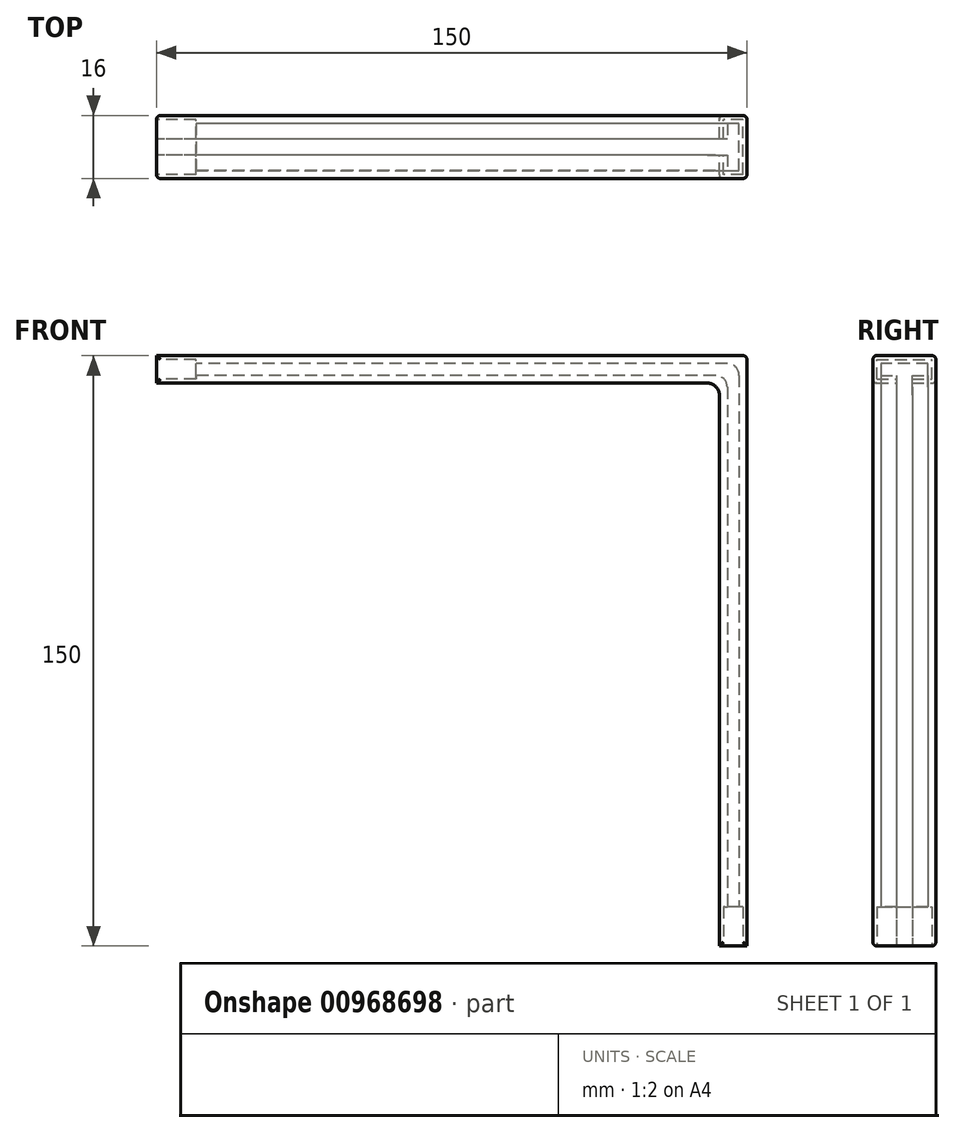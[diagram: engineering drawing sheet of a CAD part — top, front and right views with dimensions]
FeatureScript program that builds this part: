
annotation { "Feature Type Name" : "Feature", "Feature Type Description" : "" }
export const myFeature = defineFeature(function(context is Context, id is Id, definition is map)
    precondition{}
    {
        {
            var Q0;
            Q0=qCreatedBy(makeId("Front.planeOp"),FACE);
            var sketch = newSketch(context, id + "F0", { "sketchPlane" : qUnion([Q0])});
            skLineSegment(sketch, "E0", {"start": v(-19.44, 7) * mm, "end": v(130.56, 7) * mm});
            skLineSegment(sketch, "E1", {"start": v(130.56, 7) * mm, "end": v(130.56, -143) * mm});
            skLineSegment(sketch, "E2", {"start": v(130.56, -143) * mm, "end": v(123.56, -143) * mm});
            skLineSegment(sketch, "E3", {"start": v(123.56, -143) * mm, "end": v(123.56, 0) * mm});
            skLineSegment(sketch, "E4", {"start": v(123.56, 0) * mm, "end": v(-19.44, 0) * mm});
            skLineSegment(sketch, "E5", {"start": v(-19.44, 0) * mm, "end": v(-19.44, 7) * mm});
            skSolve(sketch);
        }
        {
            var Q0;
            Q0=makeQuery(id+"F0.imprint","IMPRINT",FACE,{"disambiguationData":[TD([[makeQuery(id+"F0.imprint","IMPRINT",EDGE,{"derivedFrom":sQuery(id+"F0.wireOp",EDGE,"E0")}),-1.0]])]});
            extrude(context, id + "F1", {"entities" : qUnion([Q0]), "depth" : 16 * mm, "offsetDistance" : 25 * mm});
        }
        {
            var Q0;
            Q0=makeQuery(id+"F1.opExtrude","SWEPT_FACE",FACE,{"disambiguationData":[OSD([sQuery(id+"F0.wireOp",EDGE,"E2")])]});
            var sketch = newSketch(context, id + "F2", { "sketchPlane" : qUnion([Q0])});
            skLineSegment(sketch, "E6", {"start": v(123.56, 10) * mm, "end": v(125.56, 10) * mm});
            skLineSegment(sketch, "E7", {"start": v(125.56, 10) * mm, "end": v(125.56, 14) * mm});
            skLineSegment(sketch, "E8", {"start": v(125.56, 14) * mm, "end": v(128.56, 14) * mm});
            skLineSegment(sketch, "E9", {"start": v(128.56, 14) * mm, "end": v(128.56, 2) * mm});
            skLineSegment(sketch, "E10", {"start": v(128.56, 2) * mm, "end": v(125.56, 2) * mm});
            skLineSegment(sketch, "E11", {"start": v(125.56, 2) * mm, "end": v(125.56, 6) * mm});
            skLineSegment(sketch, "E12", {"start": v(125.56, 6) * mm, "end": v(123.56, 6) * mm});
            skLineSegment(sketch, "E13", {"start": v(123.56, 6) * mm, "end": v(123.56, 10) * mm});
            skSolve(sketch);
        }
        {
            var Q0;
            Q0=makeQuery(id+"F2.imprint","IMPRINT",FACE,{"disambiguationData":[TD([[makeQuery(id+"F2.imprint","IMPRINT",EDGE,{"derivedFrom":sQuery(id+"F2.wireOp",EDGE,"E6")}),-1.0]])]});
            extrude(context, id + "F3", {"entities" : qUnion([Q0]), "operationType" : NewBodyOperationType.REMOVE, "oppositeDirection" : true, "depth" : 148 * mm, "offsetDistance" : 25 * mm});
        }
        {
            var Q0;
            Q0=makeQuery(id+"F1.opExtrude","SWEPT_FACE",FACE,{"disambiguationData":[OSD([sQuery(id+"F0.wireOp",EDGE,"E5")])]});
            var sketch = newSketch(context, id + "F4", { "sketchPlane" : qUnion([Q0])});
            skLineSegment(sketch, "E14", {"start": v(6, 0) * mm, "end": v(6, 2) * mm});
            skLineSegment(sketch, "E15", {"start": v(6, 2) * mm, "end": v(2, 2) * mm});
            skLineSegment(sketch, "E16", {"start": v(2, 2) * mm, "end": v(2, 5) * mm});
            skLineSegment(sketch, "E17", {"start": v(2, 5) * mm, "end": v(14, 5) * mm});
            skLineSegment(sketch, "E18", {"start": v(14, 5) * mm, "end": v(14, 2) * mm});
            skLineSegment(sketch, "E19", {"start": v(14, 2) * mm, "end": v(10, 2) * mm});
            skLineSegment(sketch, "E20", {"start": v(10, 2) * mm, "end": v(10, 0) * mm});
            skLineSegment(sketch, "E21", {"start": v(10, 0) * mm, "end": v(6, 0) * mm});
            skSolve(sketch);
        }
        {
            var Q0;
            Q0=makeQuery(id+"F4.imprint","IMPRINT",FACE,{"disambiguationData":[TD([[makeQuery(id+"F4.imprint","IMPRINT",EDGE,{"derivedFrom":sQuery(id+"F4.wireOp",EDGE,"E14")}),-1.0]])]});
            extrude(context, id + "F5", {"entities" : qUnion([Q0]), "operationType" : NewBodyOperationType.REMOVE, "oppositeDirection" : true, "depth" : 148 * mm, "offsetDistance" : 25 * mm});
        }
        {
            var Q0;
            Q0=makeQuery(id+"F3.boolean.opBoolean","COPY",EDGE,{"derivedFrom":makeQuery(id+"F3.opExtrude","CAP_EDGE",EDGE,{"disambiguationData":[OSD([sQuery(id+"F2.wireOp",EDGE,"E9")])],"isStart":false})});
            var Q1;
            {var subQ0=sQuery(id+"F0.wireOp",EDGE,"E3");var subQ1=makeQuery(id+"F1.opExtrude","SWEPT_FACE",FACE,{"disambiguationData":[OSD([subQ0])]});var subQ2=sQuery(id+"F0.wireOp",EDGE,"E4");var subQ3=makeQuery(id+"F1.opExtrude","SWEPT_FACE",FACE,{"disambiguationData":[OSD([subQ2])]});Q1=makeQuery(id+"F3.boolean.opBoolean","SPLIT",EDGE,{"disambiguationData":[topologyDisambiguationEdgeConnected([subQ1,subQ3]),TD([makeQuery(id+"F3.opExtrude","SWEPT_FACE",FACE,{"disambiguationData":[OSD([sQuery(id+"F2.wireOp",EDGE,"E12")])]})])],"derivedFrom":makeQuery(id+"F1.opExtrude","SWEPT_EDGE",EDGE,{"disambiguationData":[OSD([subQ0,subQ2])]})});}
            var Q2;
            {var subQ0=sQuery(id+"F0.wireOp",EDGE,"E4");var subQ1=makeQuery(id+"F1.opExtrude","SWEPT_FACE",FACE,{"disambiguationData":[OSD([subQ0])]});var subQ2=sQuery(id+"F0.wireOp",EDGE,"E3");var subQ3=makeQuery(id+"F1.opExtrude","SWEPT_FACE",FACE,{"disambiguationData":[OSD([subQ2])]});Q2=makeQuery(id+"F3.boolean.opBoolean","SPLIT",EDGE,{"disambiguationData":[topologyDisambiguationEdgeConnected([subQ3,subQ1]),TD([makeQuery(id+"F3.opExtrude","SWEPT_FACE",FACE,{"disambiguationData":[OSD([sQuery(id+"F2.wireOp",EDGE,"E6")])]})])],"derivedFrom":makeQuery(id+"F1.opExtrude","SWEPT_EDGE",EDGE,{"disambiguationData":[OSD([subQ2,subQ0])]})});}
            fillet(context, id + "F6", {"entities" : qUnion([Q0, Q1, Q2]), "radius" : 3 * mm, "tangentPropagation" : true, "allowEdgeOverflow" : false});
        }
        {
            var Q0;
            Q0=makeQuery(id+"F5.boolean.opBoolean","INTERSECT",EDGE,{"derivedFrom":[makeQuery(id+"F3.boolean.opBoolean","COPY",FACE,{"derivedFrom":makeQuery(id+"F3.opExtrude","SWEPT_FACE",FACE,{"disambiguationData":[OSD([sQuery(id+"F2.wireOp",EDGE,"E11")])]})}),makeQuery(id+"F5.opExtrude","SWEPT_FACE",FACE,{"disambiguationData":[OSD([sQuery(id+"F4.wireOp",EDGE,"E15")])]})]});
            var Q1;
            Q1=makeQuery(id+"F5.boolean.opBoolean","INTERSECT",EDGE,{"derivedFrom":[makeQuery(id+"F3.boolean.opBoolean","COPY",FACE,{"derivedFrom":makeQuery(id+"F3.opExtrude","SWEPT_FACE",FACE,{"disambiguationData":[OSD([sQuery(id+"F2.wireOp",EDGE,"E7")])]})}),makeQuery(id+"F5.opExtrude","SWEPT_FACE",FACE,{"disambiguationData":[OSD([sQuery(id+"F4.wireOp",EDGE,"E19")])]})]});
            fillet(context, id + "F7", {"entities" : qUnion([Q0, Q1]), "radius" : 3 * mm, "tangentPropagation" : true, "allowEdgeOverflow" : false});
        }
        {
            var Q0;
            Q0=makeQuery(id+"F1.opExtrude","SWEPT_EDGE",EDGE,{"disambiguationData":[OSD([sQuery(id+"F0.wireOp",EDGE,"E0"),sQuery(id+"F0.wireOp",EDGE,"E1")])]});
            var Q1;
            Q1=makeQuery(id+"F1.opExtrude","CAP_EDGE",EDGE,{"disambiguationData":[OSD([sQuery(id+"F0.wireOp",EDGE,"E0")])],"isStart":true});
            var Q2;
            Q2=makeQuery(id+"F1.opExtrude","CAP_FACE",FACE,{"disambiguationData":[OSD([sQuery(id+"F0.wireOp",EDGE,"E0"),sQuery(id+"F0.wireOp",EDGE,"E1"),sQuery(id+"F0.wireOp",EDGE,"E2"),sQuery(id+"F0.wireOp",EDGE,"E3"),sQuery(id+"F0.wireOp",EDGE,"E4"),sQuery(id+"F0.wireOp",EDGE,"E5")])],"isStart":true});
            fillet(context, id + "F8", {"entities" : qUnion([Q0, Q1, Q2]), "radius" : 1 * mm, "tangentPropagation" : true, "allowEdgeOverflow" : false});
        }
        {
            var Q0;
            Q0=makeQuery(id+"F1.opExtrude","CAP_FACE",FACE,{"disambiguationData":[OSD([sQuery(id+"F0.wireOp",EDGE,"E0"),sQuery(id+"F0.wireOp",EDGE,"E1"),sQuery(id+"F0.wireOp",EDGE,"E2"),sQuery(id+"F0.wireOp",EDGE,"E3"),sQuery(id+"F0.wireOp",EDGE,"E4"),sQuery(id+"F0.wireOp",EDGE,"E5")])],"isStart":false});
            fillet(context, id + "F9", {"entities" : qUnion([Q0]), "radius" : 1 * mm, "tangentPropagation" : true, "allowEdgeOverflow" : false});
        }
        {
            var Q0;
            Q0=makeQuery(id+"F1.opExtrude","SWEPT_FACE",FACE,{"disambiguationData":[OSD([sQuery(id+"F0.wireOp",EDGE,"E5")])]});
            var sketch = newSketch(context, id + "F10", { "sketchPlane" : qUnion([Q0])});
            skLineSegment(sketch, "E22.bottom", {"start": v(15, 1) * mm, "end": v(1, 1) * mm});
            skLineSegment(sketch, "E22.top", {"start": v(15, 6) * mm, "end": v(1, 6) * mm});
            skLineSegment(sketch, "E22.left", {"start": v(15, 1) * mm, "end": v(15, 6) * mm});
            skLineSegment(sketch, "E22.right", {"start": v(1, 1) * mm, "end": v(1, 6) * mm});
            skSolve(sketch);
        }
        {
            var Q0;
            Q0=makeQuery(id+"F10.imprint","IMPRINT",FACE,{"disambiguationData":[TD([[makeQuery(id+"F10.imprint","IMPRINT",EDGE,{"derivedFrom":sQuery(id+"F10.wireOp",EDGE,"E22.top")}),1.0]])]});
            extrude(context, id + "F11", {"entities" : qUnion([Q0]), "operationType" : NewBodyOperationType.REMOVE, "oppositeDirection" : true, "depth" : 10 * mm, "offsetDistance" : 25 * mm});
        }
        {
            var Q0;
            Q0=makeQuery(id+"F1.opExtrude","SWEPT_FACE",FACE,{"disambiguationData":[OSD([sQuery(id+"F0.wireOp",EDGE,"E2")])]});
            var sketch = newSketch(context, id + "F12", { "sketchPlane" : qUnion([Q0])});
            skLineSegment(sketch, "E23.bottom", {"start": v(124.56, 15) * mm, "end": v(129.56, 15) * mm});
            skLineSegment(sketch, "E23.top", {"start": v(124.56, 1) * mm, "end": v(129.56, 1) * mm});
            skLineSegment(sketch, "E23.left", {"start": v(124.56, 15) * mm, "end": v(124.56, 1) * mm});
            skLineSegment(sketch, "E23.right", {"start": v(129.56, 15) * mm, "end": v(129.56, 1) * mm});
            skSolve(sketch);
        }
        {
            var Q0;
            {var subQ2=sQuery(id+"F12.wireOp",EDGE,"E23.bottom");Q0=makeQuery(id+"F12.imprint","IMPRINT",FACE,{"disambiguationData":[TD([[makeQuery(id+"F12.imprint","IMPRINT",EDGE,{"derivedFrom":subQ2}),1.0]])]});}
            extrude(context, id + "F13", {"entities" : qUnion([Q0]), "operationType" : NewBodyOperationType.REMOVE, "oppositeDirection" : true, "depth" : 10 * mm, "offsetDistance" : 25 * mm});
        }
    });
